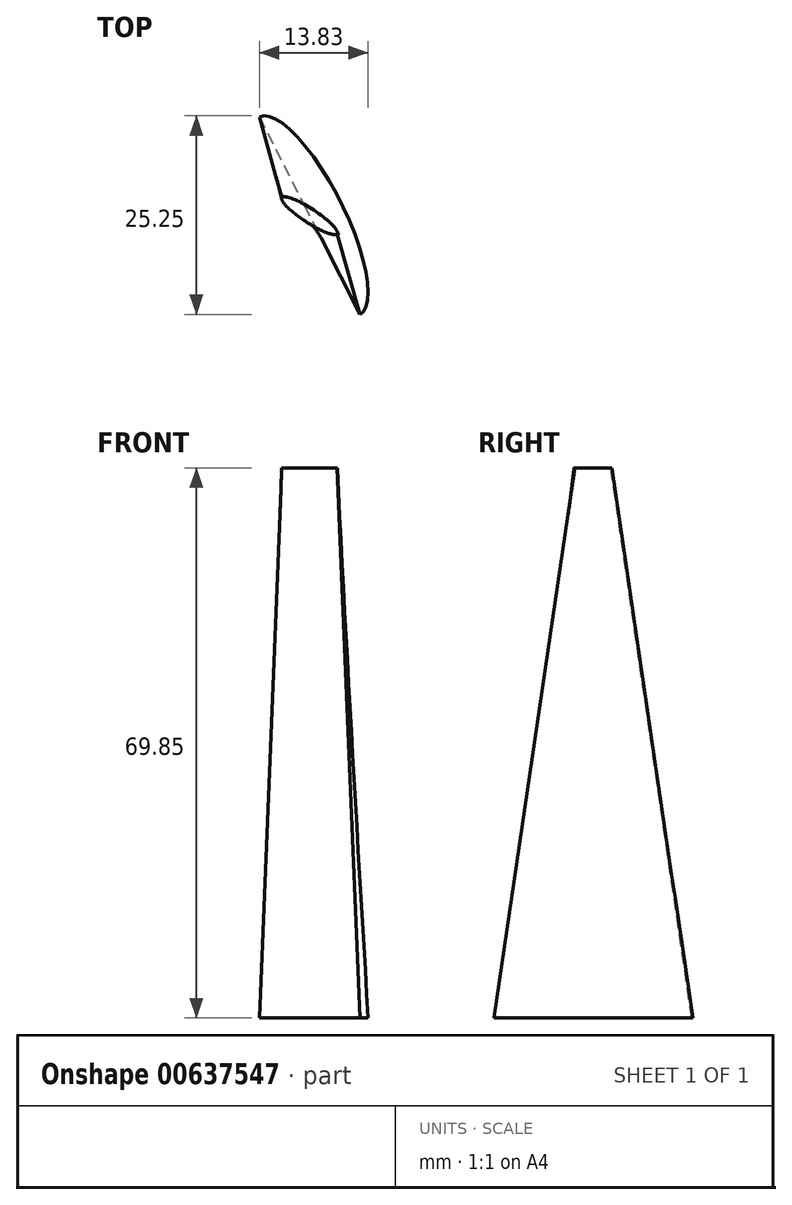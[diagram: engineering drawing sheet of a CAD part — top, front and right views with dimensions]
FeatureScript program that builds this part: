
annotation { "Feature Type Name" : "Feature", "Feature Type Description" : "" }
export const myFeature = defineFeature(function(context is Context, id is Id, definition is map)
    precondition{}
    {
        {
            var Q0;
            Q0=qCreatedBy(makeId("Top.planeOp"),FACE);
            cPlane(context, id + "F0", {"entities" : qUnion([Q0]), "cplaneType" : CPlaneType.OFFSET, "offset" : 6.35 * mm, "width" : 152.4 * mm, "height" : 152.4 * mm});
        }
        {
            var Q0;
            Q0=qCreatedBy(id+"F0.planeOp",FACE);
            cPlane(context, id + "F1", {"entities" : qUnion([Q0]), "cplaneType" : CPlaneType.OFFSET, "offset" : 6.35 * mm, "width" : 152.4 * mm, "height" : 152.4 * mm});
        }
        {
            var Q0;
            Q0=qCreatedBy(id+"F1.planeOp",FACE);
            cPlane(context, id + "F2", {"entities" : qUnion([Q0]), "cplaneType" : CPlaneType.OFFSET, "offset" : 6.35 * mm, "width" : 152.4 * mm, "height" : 152.4 * mm});
        }
        {
            var Q0;
            Q0=qCreatedBy(id+"F2.planeOp",FACE);
            cPlane(context, id + "F3", {"entities" : qUnion([Q0]), "cplaneType" : CPlaneType.OFFSET, "offset" : 6.35 * mm, "width" : 152.4 * mm, "height" : 152.4 * mm});
        }
        {
            var Q0;
            Q0=qCreatedBy(id+"F3.planeOp",FACE);
            cPlane(context, id + "F4", {"entities" : qUnion([Q0]), "cplaneType" : CPlaneType.OFFSET, "offset" : 6.35 * mm, "width" : 152.4 * mm, "height" : 152.4 * mm});
        }
        {
            var Q0;
            Q0=qCreatedBy(id+"F4.planeOp",FACE);
            cPlane(context, id + "F5", {"entities" : qUnion([Q0]), "cplaneType" : CPlaneType.OFFSET, "offset" : 6.35 * mm, "width" : 152.4 * mm, "height" : 152.4 * mm});
        }
        {
            var Q0;
            Q0=qCreatedBy(id+"F5.planeOp",FACE);
            cPlane(context, id + "F6", {"entities" : qUnion([Q0]), "cplaneType" : CPlaneType.OFFSET, "offset" : 6.35 * mm, "width" : 152.4 * mm, "height" : 152.4 * mm});
        }
        {
            var Q0;
            Q0=qCreatedBy(id+"F6.planeOp",FACE);
            cPlane(context, id + "F7", {"entities" : qUnion([Q0]), "cplaneType" : CPlaneType.OFFSET, "offset" : 6.35 * mm, "width" : 152.4 * mm, "height" : 152.4 * mm});
        }
        {
            var Q0;
            Q0=qCreatedBy(id+"F7.planeOp",FACE);
            cPlane(context, id + "F8", {"entities" : qUnion([Q0]), "cplaneType" : CPlaneType.OFFSET, "offset" : 6.35 * mm, "width" : 152.4 * mm, "height" : 152.4 * mm});
        }
        {
            var Q0;
            Q0=qCreatedBy(id+"F8.planeOp",FACE);
            cPlane(context, id + "F9", {"entities" : qUnion([Q0]), "cplaneType" : CPlaneType.OFFSET, "offset" : 6.35 * mm, "width" : 152.4 * mm, "height" : 152.4 * mm});
        }
        {
            var Q0;
            Q0=qCreatedBy(id+"F9.planeOp",FACE);
            cPlane(context, id + "F10", {"entities" : qUnion([Q0]), "cplaneType" : CPlaneType.OFFSET, "offset" : 6.35 * mm, "width" : 152.4 * mm, "height" : 152.4 * mm});
        }
        {
            var Q0;
            Q0=qCreatedBy(id+"F10.planeOp",FACE);
            cPlane(context, id + "F11", {"entities" : qUnion([Q0]), "cplaneType" : CPlaneType.OFFSET, "offset" : 6.35 * mm, "width" : 152.4 * mm, "height" : 152.4 * mm});
        }
        {
            var Q0;
            Q0=qCreatedBy(makeId("Right.planeOp"),FACE);
            var sketch = newSketch(context, id + "F12", { "sketchPlane" : qUnion([Q0])});
            skLineSegment(sketch, "E0", {"start": v(12.7, 6.35) * mm, "end": v(-12.7, 6.35) * mm});
            skPoint(sketch, "E1", {"position": v(0, 6.35) * mm});
            skLineSegment(sketch, "E2", {"start": v(2.12, 76.2) * mm, "end": v(-2.12, 76.2) * mm});
            skPoint(sketch, "E3", {"position": v(0, 76.2) * mm});
            skLineSegment(sketch, "E4", {"start": v(-2.12, 76.2) * mm, "end": v(-12.7, 6.35) * mm});
            skLineSegment(sketch, "E5", {"start": v(2.12, 76.2) * mm, "end": v(12.7, 6.35) * mm});
            skPoint(sketch, "E6", {"position": v(11.74, 12.7) * mm});
            skPoint(sketch, "E7", {"position": v(10.78, 19.05) * mm});
            skPoint(sketch, "E8", {"position": v(9.81, 25.4) * mm});
            skPoint(sketch, "E9", {"position": v(8.85, 31.75) * mm});
            skPoint(sketch, "E10", {"position": v(7.89, 38.1) * mm});
            skPoint(sketch, "E11", {"position": v(6.93, 44.45) * mm});
            skPoint(sketch, "E12", {"position": v(5.97, 50.8) * mm});
            skPoint(sketch, "E13", {"position": v(5, 57.15) * mm});
            skPoint(sketch, "E14", {"position": v(4.04, 63.5) * mm});
            skPoint(sketch, "E15", {"position": v(3.08, 69.85) * mm});
            skSolve(sketch);
        }
        {
            var Q0;
            Q0=qCreatedBy(makeId("Top.planeOp"),FACE);
            var sketch = newSketch(context, id + "F13", { "sketchPlane" : qUnion([Q0])});
            skPoint(sketch, "E16.0", {"position": v(0, 12.7) * mm});
            skPoint(sketch, "E17.0", {"position": v(0, -12.7) * mm});
            skLineSegment(sketch, "E18", {"start": v(-51.06, 12.7) * mm, "end": v(60.83, 12.7) * mm});
            skLineSegment(sketch, "E19", {"start": v(-49.79, -12.7) * mm, "end": v(63.01, -12.7) * mm});
            skPoint(sketch, "E20.0", {"position": v(0, 11.74) * mm});
            skPoint(sketch, "E21.0", {"position": v(0, 10.78) * mm});
            skPoint(sketch, "E22.0", {"position": v(0, 9.81) * mm});
            skPoint(sketch, "E23.0", {"position": v(0, 8.85) * mm});
            skPoint(sketch, "E24.0", {"position": v(0, 7.89) * mm});
            skPoint(sketch, "E25.0", {"position": v(0, 6.93) * mm});
            skPoint(sketch, "E26.0", {"position": v(0, 5.97) * mm});
            skPoint(sketch, "E27.0", {"position": v(0, 5) * mm});
            skPoint(sketch, "E28.0", {"position": v(0, 4.04) * mm});
            skPoint(sketch, "E29.0", {"position": v(0, 3.08) * mm});
            skPoint(sketch, "E30.0", {"position": v(0, 2.12) * mm});
            skLineSegment(sketch, "E31", {"start": v(0, 11.74) * mm, "end": v(-28.18, 11.74) * mm});
            skLineSegment(sketch, "E32", {"start": v(0, 10.78) * mm, "end": v(-29.4, 10.78) * mm});
            skLineSegment(sketch, "E33", {"start": v(0, 9.81) * mm, "end": v(-30.69, 9.81) * mm});
            skLineSegment(sketch, "E34", {"start": v(0, 8.85) * mm, "end": v(-32.79, 8.85) * mm});
            skLineSegment(sketch, "E35", {"start": v(0, 7.89) * mm, "end": v(-33.76, 7.89) * mm});
            skLineSegment(sketch, "E36", {"start": v(0, 6.93) * mm, "end": v(-35.38, 6.93) * mm});
            skLineSegment(sketch, "E37", {"start": v(0, 5.97) * mm, "end": v(-40.56, 5.97) * mm});
            skLineSegment(sketch, "E38", {"start": v(0, 5) * mm, "end": v(-43.8, 5) * mm});
            skLineSegment(sketch, "E39", {"start": v(0, 4.04) * mm, "end": v(-44.84, 4.04) * mm});
            skLineSegment(sketch, "E40", {"start": v(0, 3.08) * mm, "end": v(-48.8, 3.08) * mm});
            skLineSegment(sketch, "E41", {"start": v(0, 2.12) * mm, "end": v(-50.1, 2.12) * mm});
            skPoint(sketch, "E42", {"position": v(0, 13.66) * mm});
            skLineSegment(sketch, "E43", {"start": v(0, 13.66) * mm, "end": v(-11.96, 13.66) * mm});
            skSolve(sketch);
        }
        {
            var Q0;
            Q0=qCreatedBy(id+"F0.planeOp",FACE);
            var sketch = newSketch(context, id + "F14", { "sketchPlane" : qUnion([Q0])});
            skLineSegment(sketch, "E44.0", {"start": v(-51.06, 12.7) * mm, "end": v(60.83, 12.7) * mm});
            skEllipse(sketch, "E45", {"center": v(0, 0) * mm, "majorRadius": 14.08 * mm, "minorRadius": 4.3 * mm, "majorAxis": v(-0.45, 0.9)});
            skLineSegment(sketch, "E46", {"start": v(-6.38, 12.55) * mm, "end": v(6.38, -12.55) * mm});
            skSolve(sketch);
        }
        {
            var Q0;
            Q0=qCreatedBy(id+"F11.planeOp",FACE);
            var sketch = newSketch(context, id + "F15", { "sketchPlane" : qUnion([Q0])});
            skEllipse(sketch, "E47", {"center": v(0, 0) * mm, "majorRadius": 4.18 * mm, "minorRadius": 0.89 * mm, "majorAxis": v(-0.84, 0.55)});
            skLineSegment(sketch, "E48", {"start": v(-3.5, 2.28) * mm, "end": v(3.5, -2.28) * mm});
            skSolve(sketch);
        }
        {
            var Q0;
            Q0=makeQuery(id+"F14.imprint","IMPRINT",FACE,{"disambiguationData":[TD([[makeQuery(id+"F14.imprint","IMPRINT",EDGE,{"derivedFrom":sQuery(id+"F14.wireOp",EDGE,"E45")}),1.0]])]});
            var Q1;
            Q1=makeQuery(id+"F15.imprint","IMPRINT",FACE,{"disambiguationData":[TD([[makeQuery(id+"F15.imprint","IMPRINT",EDGE,{"derivedFrom":sQuery(id+"F15.wireOp",EDGE,"E47")}),1.0]])]});
            loft(context, id + "F16", {"sheetProfilesArray" : [{ "sheetProfileEntities" : qUnion([Q0]) }, { "sheetProfileEntities" : qUnion([Q1]) }]});
        }
        {
            var Q0;
            Q0=makeQuery(id+"F16.opLoft","CAP_FACE",FACE,{"disambiguationData":[OSD([makeQuery(id+"F14.imprint","IMPRINT",FACE,{"disambiguationData":[TD([[makeQuery(id+"F14.imprint","IMPRINT",EDGE,{"derivedFrom":sQuery(id+"F14.wireOp",EDGE,"E45")}),1.0]])]})])],"isStart":true});
            var sketch = newSketch(context, id + "F17", { "sketchPlane" : qUnion([Q0])});
            skCircle(sketch, "E49", {"center": v(0, 0) * mm, "radius": 1.52 * mm});
            skSolve(sketch);
        }
        {
            var Q0;
            Q0=qSketchRegion(id+"F17",true);
            extrude(context, id + "F18", {"entities" : qUnion([Q0]), "operationType" : NewBodyOperationType.REMOVE, "oppositeDirection" : true, "depth" : 1 / 101.6 * mm, "offsetDistance" : 25.4 * mm});
        }
    });
